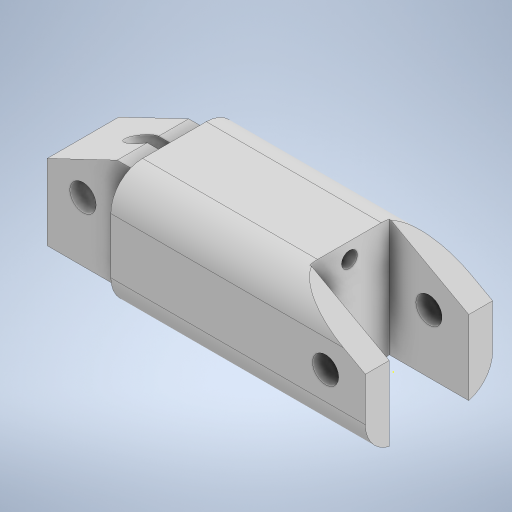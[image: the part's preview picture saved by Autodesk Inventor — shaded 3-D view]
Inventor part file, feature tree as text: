
AUTODESK INVENTOR PART (.ipt)
format: ipt  version: 2024 (Build 280153000, 153)  size: 460,288 bytes
history: native  units: mm
features: sketch x21, extrude x18, chamfer x3, move_body x3, plane x2, split x2, boolean_combine x1, fillet x1
ambient origin geometry x8: Origin, YZ Plane, XZ Plane, XY Plane, X Axis, Y Axis, Z Axis, Center Point
bodies: Solid1 (feature_tree), Solid2 (feature_tree), Solid3 (feature_tree), Solid4 (feature_tree), Solid5 (feature_tree)
feature tree (51):
  extrude  "Extrusion1"  Depth=16.0mm
  sketch  "Sketch2"  dims[d2=15.0mm d3=0.0mm d4=10.0mm]
  extrude  "Extrusion2"  Depth=10.0mm
  chamfer  "Chamfer1"  Distance=21.25mm
  extrude  "Extrusion3"  Depth=10.0mm TaperAngle=0.0deg
  extrude  "Extrusion4"  Depth=11.5mm TaperAngle=0.0deg
  extrude  "Extrusion5"  Depth=1.0mm TaperAngle=0.0deg
  chamfer  "Chamfer2"  Distance=6.0mm Angle=45.0deg
  sketch  "Sketch6"  dims[d14=7.0mm d15=11.5mm d16=0.0mm]
  extrude  "Extrusion6"  Depth=9.0mm
  extrude  "Extrusion7"  Depth=11.5mm TaperAngle=0.0deg
  chamfer  "Chamfer3"  Distance=11.5mm Angle=45.0deg
  sketch  "Sketch9"  dims[d26=3.3mm d27=45.25mm d28=0.0mm d29=11.5mm d30=5.5mm d31=45.0deg]
  extrude  "Extrusion8"  Depth=65.75mm TaperAngle=0.0deg
  extrude  "Extrusion9"  Depth=9.0mm TaperAngle=0.0deg
  extrude  "Extrusion10"  Depth=13.0mm TaperAngle=0.0deg
  sketch  "Sketch13"  dims[d43=24.0mm d44=21.0mm d45=0.0mm]
  extrude  "Extrusion11"  Depth=21.0mm TaperAngle=0.0deg
  extrude  "Extrusion12"  TaperAngle=0.0deg  [1 undecoded]
  extrude  "Extrusion13"  Depth=6.0mm TaperAngle=0.0deg
  plane  "Work Plane1"
  split  "Split1"
  move_body  "Move Body1"
  extrude  "Extrusion14"  Depth=10.0mm TaperAngle=0.0deg
  move_body  "Move Body2"
  extrude  "Extrusion15"  TaperAngle=0.0deg  [1 undecoded]
  plane  "Work Plane2"
  split  "Split2"
  move_body  "Move Body3"
  boolean_combine  "Combine1"
  fillet  "Fillet2"  Radius=4.0mm
  extrude  "Extrusion16"  Depth=0.5mm TaperAngle=0.0deg
  extrude  "Extrusion17"  Depth=10.0mm TaperAngle=0.0deg
  extrude  "Extrusion19"  [1 undecoded]
  sketch  "Sketch1"  dims[d0=36.0mm d1=16.0mm]
  sketch  "Sketch3"  dims[d5=10.0mm]
  sketch  "Sketch4"  dims[d6=3.3mm d7=21.25mm d8=0.0mm]
  sketch  "Sketch5"  dims[d9=10.0mm d10=5.5mm d11=45.0deg d12=10.0mm d13=0.0mm]
  sketch  "Sketch7"  dims[d17=3.3mm d18=1.0mm d19=0.0mm d20=6.0mm d21=11.5mm d22=45.0deg]
  sketch  "Sketch8"  dims[d23=15.0mm d24=0.0mm d25=9.0mm]
  sketch  "Sketch10"  dims[d32=2.0mm d33=65.75mm d34=0.0mm]
  sketch  "Sketch11"  dims[d35=0.5mm d36=0.0mm d37=9.0mm d38=0.0mm]
  sketch  "Sketch12"  dims[d39=0.5mm d40=0.0mm d41=13.0mm d42=0.0mm]
  sketch  "Sketch14"  dims[d46=12.25mm d47=-12.0mm d48=0.0mm d49=0.0mm]
  sketch  "Sketch15"  dims[d50=30.0mm d51=0.0mm d52=6.0mm d53=0.0mm d54=0.0mm]
  sketch  "Sketch16"  dims[d56=10.0mm d57=20.0mm d58=0.0mm]
  sketch  "Sketch17"  dims[d59=3.75mm d60=-10.0mm d61=0.0mm d62=0.0mm d63=4.0mm]
  sketch  "Sketch18"  dims[d64=0.5mm d65=0.0mm d66=0.5mm d67=0.0mm]
  sketch  "Sketch19"  dims[d71=3.0mm d72=10.0mm d73=0.0mm]
  sketch  "Sketch20"
  sketch  "Sketch22"
note: 3 required parameter values undecoded (feature->parameter linkage not recoverable at this tier; creation-order binding heuristic only, values carry confidence <= 0.55)
